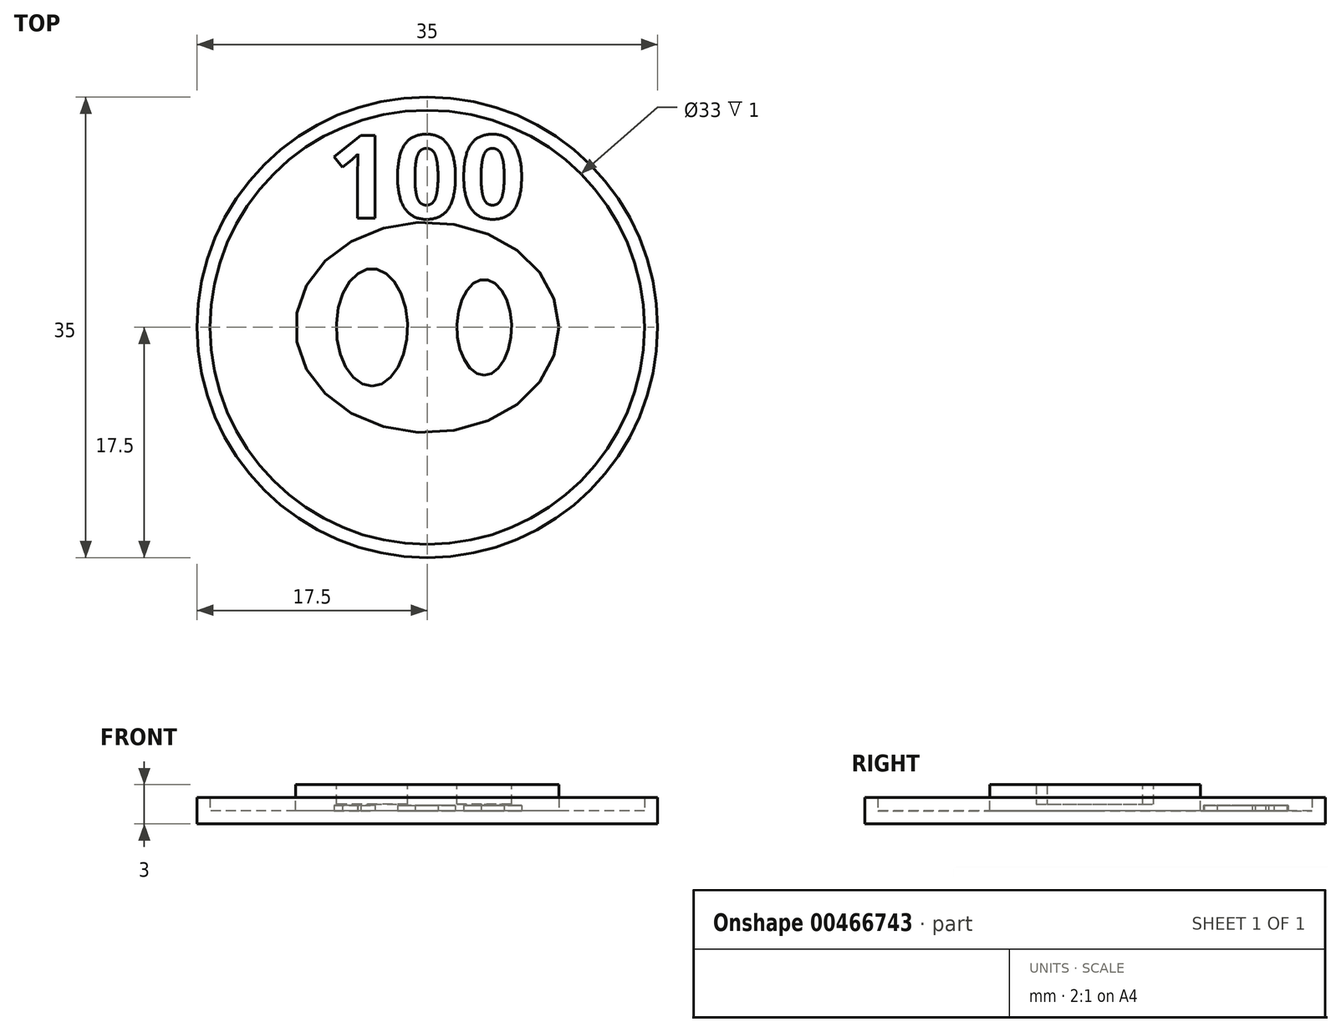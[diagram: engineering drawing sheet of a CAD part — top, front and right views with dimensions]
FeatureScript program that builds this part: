
annotation { "Feature Type Name" : "Feature", "Feature Type Description" : "" }
export const myFeature = defineFeature(function(context is Context, id is Id, definition is map)
    precondition{}
    {
        {
            var Q0;
            Q0=qCreatedBy(makeId("Top.planeOp"),FACE);
            var sketch = newSketch(context, id + "F0", { "sketchPlane" : qUnion([Q0])});
            skCircle(sketch, "E0", {"center": v(0, 0) * mm, "radius": 17.5 * mm});
            skCircle(sketch, "E1", {"center": v(0, 0) * mm, "radius": 16.5 * mm});
            skEllipse(sketch, "E2", {"center": v(0, 0) * mm, "majorRadius": 10 * mm, "minorRadius": 8 * mm, "majorAxis": v(1, 0)});
            skEllipse(sketch, "E3", {"center": v(-4.2, 0) * mm, "majorRadius": 4.46 * mm, "minorRadius": 2.7 * mm, "majorAxis": v(0, -1)});
            skEllipse(sketch, "E4", {"center": v(4.33, 0) * mm, "majorRadius": 3.63 * mm, "minorRadius": 2.07 * mm, "majorAxis": v(0, -1)});
            skSolve(sketch);
        }
        {
            var Q0;
            Q0=makeQuery(id+"F0.imprint","IMPRINT",FACE,{"disambiguationData":[TD([[makeQuery(id+"F0.imprint","IMPRINT",EDGE,{"derivedFrom":sQuery(id+"F0.wireOp",EDGE,"E0")}),1.0]])]});
            extrude(context, id + "F1", {"entities" : qUnion([Q0]), "depth" : 2 * mm});
        }
        {
            var Q0;
            Q0=makeQuery(id+"F0.imprint","IMPRINT",FACE,{"disambiguationData":[TD([[makeQuery(id+"F0.imprint","IMPRINT",EDGE,{"derivedFrom":sQuery(id+"F0.wireOp",EDGE,"E2")}),1.0]])]});
            extrude(context, id + "F2", {"entities" : qUnion([Q0]), "operationType" : NewBodyOperationType.ADD, "depth" : 3 * mm});
        }
        {
            var Q0;
            Q0=makeQuery(id+"F0.imprint","IMPRINT",FACE,{"disambiguationData":[TD([[makeQuery(id+"F0.imprint","IMPRINT",EDGE,{"derivedFrom":sQuery(id+"F0.wireOp",EDGE,"E3")}),1.0]])]});
            var Q1;
            Q1=makeQuery(id+"F0.imprint","IMPRINT",FACE,{"disambiguationData":[TD([[makeQuery(id+"F0.imprint","IMPRINT",EDGE,{"derivedFrom":sQuery(id+"F0.wireOp",EDGE,"E4")}),1.0]])]});
            extrude(context, id + "F3", {"entities" : qUnion([Q0, Q1]), "operationType" : NewBodyOperationType.ADD, "depth" : 1.5 * mm});
        }
        {
            var Q0;
            Q0=makeQuery(id+"F0.imprint","IMPRINT",FACE,{"disambiguationData":[TD([[makeQuery(id+"F0.imprint","IMPRINT",EDGE,{"derivedFrom":sQuery(id+"F0.wireOp",EDGE,"E1")}),1.0]])]});
            extrude(context, id + "F4", {"entities" : qUnion([Q0]), "operationType" : NewBodyOperationType.ADD, "depth" : 1 * mm});
        }
        {
            var Q0;
            Q0=makeQuery(id+"F4.opExtrude","CAP_FACE",FACE,{"disambiguationData":[OSD([sQuery(id+"F0.wireOp",EDGE,"E1"),sQuery(id+"F0.wireOp",EDGE,"E2")])],"isStart":false});
            var sketch = newSketch(context, id + "F5", { "sketchPlane" : qUnion([Q0])});
            skText(sketch, "E5", { "text": "100", "fontName": "OpenSans-Bold.ttf"});
            const initialGuessF5  = {"E5": [-0.0076, 0.0083, 1, 0, 0.00634]};
            skSetInitialGuess(sketch, initialGuessF5);
            skSolve(sketch);
        }
        {
            var Q0;
            Q0 = qSketchRegion(id + "F5", true);
            extrude(context, id + "F6", {"entities" : qUnion([Q0]), "operationType" : NewBodyOperationType.ADD, "depth" : .4 * mm});
        }
    });
